FCSTD DOCUMENT  (FreeCAD 0.17R10993 (Git))
Label: heelsv3
License: All rights reserved
LicenseURL: http://en.wikipedia.org/wiki/All_rights_reserved
objects: Image::ImagePlane×1, Sketcher::SketchObject×1
note: 1 computed .brp shape members not serialized (recipe doc carries the construction recipe); baked Part::Feature solids carry a one-line shape summary decoded from their .brp

FEATURE [Image::ImagePlane] ImagePlane
  Placement = pos=(103.2,48.5,-0.1) rot=(0,0,1;0rad)
  XSize = 226.207
  YSize = 153
FEATURE [Sketcher::SketchObject] Sketch001
  sketch-geometry (12):
    g0: ArcOfCircle [constr] CenterX=15 CenterY=-0.955 CenterZ=0 NormalX=0 NormalY=0 NormalZ=1 Radius=140.003 StartAngle=0.00682132 EndAngle=0.805375
    g1-g6: Circle [constr] x6 (B-spline internal-alignment scaffolding for g7; pole/knot coordinates omitted)
    g7: BSplineCurve PolesCount=6 KnotsCount=4 Degree=3 IsPeriodic=0
    g8-g11: GeomPoint [constr] x4 (B-spline internal-alignment scaffolding for g7; pole/knot coordinates omitted)
  constraints (11):
    c: PointOnObject(g0,g-1)
    c: DistanceX(g0) = 112
    c: DistanceY(g0) = 100
    c: DistanceX(g0) = 155
    c: DistanceX(g0) = 15
    c: Coincident(g1,g-1)
    c: Radius(g1) = 5
    c: Equal(g1, g2-g6) x5
    c: Coincident(g6,g0)
    c: InternalAlignment(g1-g6 -> g7) x6
    c: InternalAlignment(g8-g11 -> g7) x4
